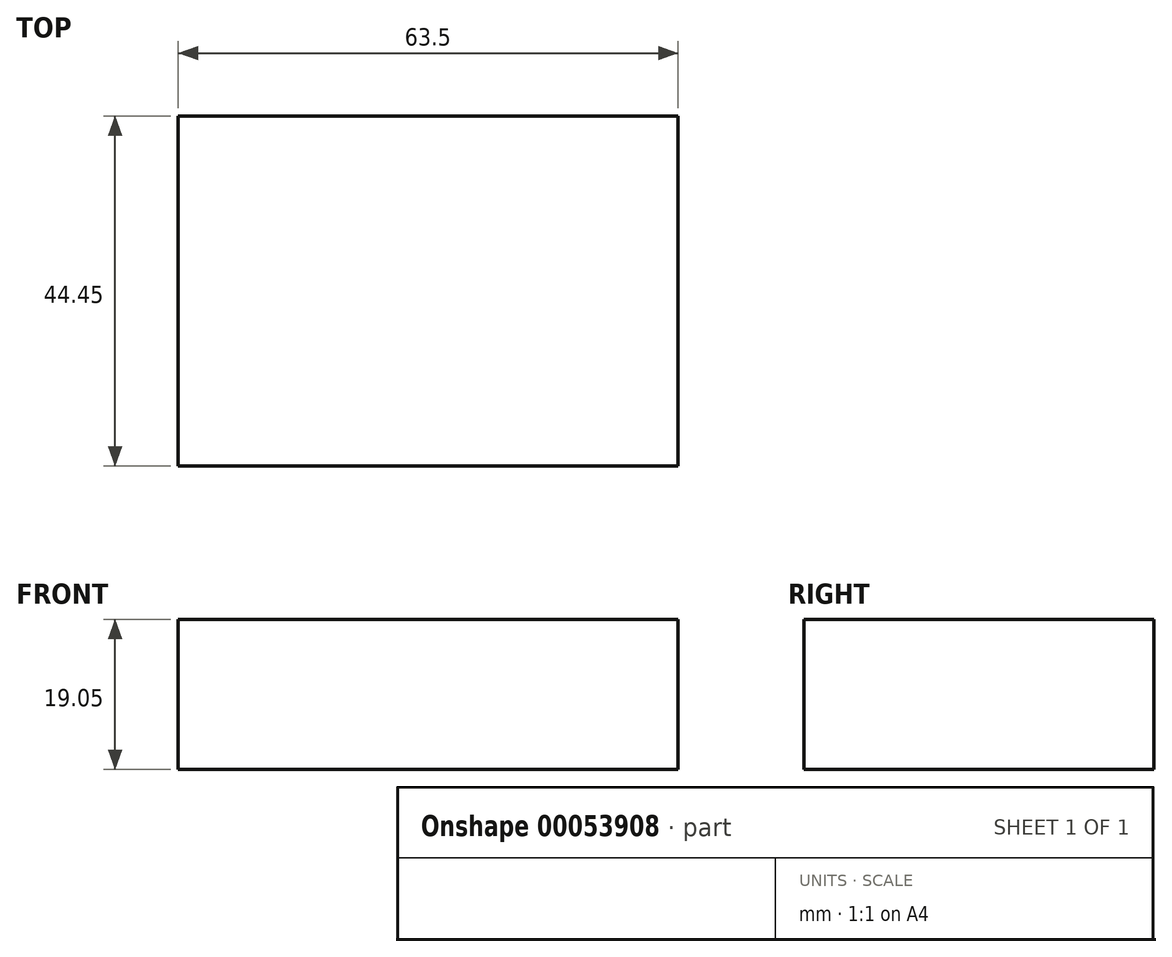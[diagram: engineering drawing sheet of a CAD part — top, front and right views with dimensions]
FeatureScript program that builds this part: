
annotation { "Feature Type Name" : "Feature", "Feature Type Description" : "" }
export const myFeature = defineFeature(function(context is Context, id is Id, definition is map)
    precondition{}
    {
        {
            var Q0;
            Q0=qCreatedBy(makeId("Front.planeOp"),FACE);
            var sketch = newSketch(context, id + "F0", { "sketchPlane" : qUnion([Q0])});
            skLineSegment(sketch, "E0.bottom", {"start": v(-20.86, 7.11) * mm, "end": v(42.64, 7.11) * mm});
            skLineSegment(sketch, "E0.top", {"start": v(-20.86, -11.94) * mm, "end": v(42.64, -11.94) * mm});
            skLineSegment(sketch, "E0.left", {"start": v(-20.86, 7.11) * mm, "end": v(-20.86, -11.94) * mm});
            skLineSegment(sketch, "E0.right", {"start": v(42.64, 7.11) * mm, "end": v(42.64, -11.94) * mm});
            skSolve(sketch);
        }
        {
            var Q0;
            Q0 = qSketchRegion(id + "F0", true);
            extrude(context, id + "F1", {"entities" : qUnion([Q0]), "depth" : 44.45 * mm});
        }
    });
